# Revit family: SS-Digitally Printed Wall Art-Inpro
name_source: partatom
category: Generic Models
revit_build: Autodesk Revit 2018 (Build: 20170223_1515(x64)
units: mm (PartAtom-declared; Revit-internal decimal feet)

## family parameters
Always vertical = Yes
Can host rebar = No
Cut with Voids When Loaded = No
Part Type = Normal
Room Calculation Point = No
Round Connector Dimension = Use Diameter
Shared = No
Work Plane-Based = No

## types (13) — shared parameters
Description = Digitally Printed Wall Art, .060in thickness, Matte Finish
ISO BIM# = BIMSS.007
Manufacturer = Inpro®
Model = Digitally Printed Wall Art
URL = https://www.inprocorp.com

## per-type parameters (varying)
| type | Custom Size | Standard Height | Standard Size | Standard Width | Type Comments |
| 23" x 23" | No | 1' - 11" | Yes | 1' - 11" | Standard Size; 23"x23" |
| 23" x 46" | No | 1' - 11" | Yes | 3' - 10" | Standard Size; 23"x46" |
| 23" x 71" | No | 1' - 11" | Yes | 5' - 11" | Standard Size; 23"x71" |
| 23" x 94" | No | 1' - 11" | Yes | 7' - 10" | Standard Size; 23"x94" |
| 46" x 46" | No | 3' - 10" | Yes | 3' - 10" | Standard Size; 46"x46" |
| 46" x 71" | No | 3' - 10" | Yes | 5' - 11" | Standard Size; 46"x71" |
| 31" x 46" | No | 3' - 10" | Yes | 5' - 11" | Standard Size; 31"x46" |
| 94" x 23" | No | 7' - 10" | Yes | 1' - 11" | Standard Size; 94"x23" |
| 71" x 46" | No | 5' - 11" | Yes | 3' - 10" | Standard Size; 71"x46" |
| 71" x 23" | No | 5' - 11" | Yes | 1' - 11" | Standard Size; 71"x23" |
| 46" x 31" | No | 3' - 10" | Yes | 2' - 7" | Standard Size; 46"x31" |
| 46" x 23" | No | 3' - 10" | Yes | 1' - 11" | Standard Size; 46"x23" |
| Custom | Yes | 1' - 11" | No | 1' - 11" | Custom Size |

## geometry (parser evidence)
native form markers: Sweep x1
no freeform markers — native parametric forms only
